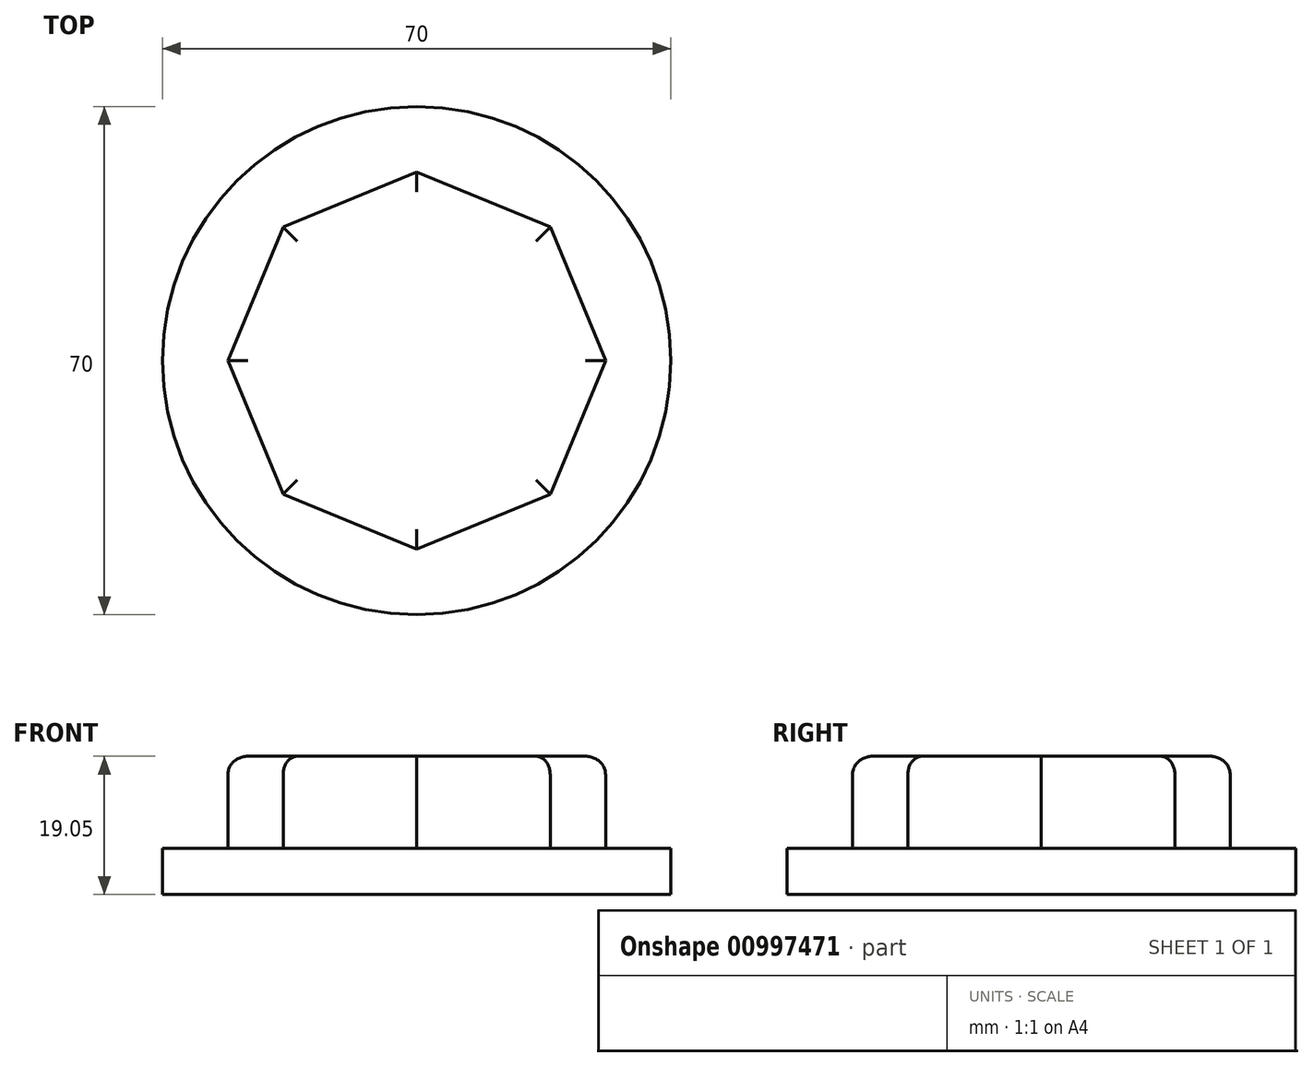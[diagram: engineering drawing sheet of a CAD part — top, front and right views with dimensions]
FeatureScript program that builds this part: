
annotation { "Feature Type Name" : "Feature", "Feature Type Description" : "" }
export const myFeature = defineFeature(function(context is Context, id is Id, definition is map)
    precondition{}
    {
        {
            var Q0;
            Q0=qCreatedBy(makeId("Top.planeOp"),FACE);
            var sketch = newSketch(context, id + "F0", { "sketchPlane" : qUnion([Q0])});
            skCircle(sketch, "E0", {"center": v(0, 0) * mm, "radius": 35 * mm});
            skSolve(sketch);
        }
        {
            var Q0;
            Q0 = qSketchRegion(id + "F0", true);
            extrude(context, id + "F1", {"entities" : qUnion([Q0]), "depth" : 6.35 * mm, "offsetDistance" : 25.4 * mm});
        }
        {
            var Q0;
            Q0=makeQuery(id+"F1.opExtrude","CAP_FACE",FACE,{"disambiguationData":[OSD([sQuery(id+"F0.wireOp",EDGE,"E0")])],"isStart":false});
            var sketch = newSketch(context, id + "F2", { "sketchPlane" : qUnion([Q0])});
            skCircle(sketch, "E1.cCircle", {"center": v(0, 0) * mm, "radius": 26 * mm, "construction": true});
            skLineSegment(sketch, "E1.0", {"start": v(26, 0) * mm, "end": v(18.38, -18.38) * mm});
            skLineSegment(sketch, "E1.1", {"start": v(18.38, -18.38) * mm, "end": v(0, -26) * mm});
            skLineSegment(sketch, "E1.2", {"start": v(0, -26) * mm, "end": v(-18.38, -18.38) * mm});
            skLineSegment(sketch, "E1.3", {"start": v(-18.38, -18.38) * mm, "end": v(-26, 0) * mm});
            skLineSegment(sketch, "E1.4", {"start": v(-26, 0) * mm, "end": v(-18.38, 18.38) * mm});
            skLineSegment(sketch, "E1.5", {"start": v(-18.38, 18.38) * mm, "end": v(0, 26) * mm});
            skLineSegment(sketch, "E1.6", {"start": v(0, 26) * mm, "end": v(18.38, 18.38) * mm});
            skLineSegment(sketch, "E1.7", {"start": v(18.38, 18.38) * mm, "end": v(26, 0) * mm});
            skSolve(sketch);
        }
        {
            var Q0;
            Q0 = qSketchRegion(id + "F2", true);
            extrude(context, id + "F3", {"entities" : qUnion([Q0]), "operationType" : NewBodyOperationType.ADD, "depth" : 12.7 * mm, "offsetDistance" : 25.4 * mm});
        }
        {
            var Q0;
            Q0=makeQuery(id+"F3.opExtrude","CAP_EDGE",EDGE,{"disambiguationData":[OSD([sQuery(id+"F2.wireOp",EDGE,"E1.0")])],"isStart":false});
            var Q1;
            Q1=makeQuery(id+"F3.opExtrude","CAP_EDGE",EDGE,{"disambiguationData":[OSD([sQuery(id+"F2.wireOp",EDGE,"E1.7")])],"isStart":false});
            var Q2;
            Q2=makeQuery(id+"F3.opExtrude","CAP_EDGE",EDGE,{"disambiguationData":[OSD([sQuery(id+"F2.wireOp",EDGE,"E1.6")])],"isStart":false});
            var Q3;
            Q3=makeQuery(id+"F3.opExtrude","CAP_EDGE",EDGE,{"disambiguationData":[OSD([sQuery(id+"F2.wireOp",EDGE,"E1.5")])],"isStart":false});
            var Q4;
            Q4=makeQuery(id+"F3.opExtrude","CAP_EDGE",EDGE,{"disambiguationData":[OSD([sQuery(id+"F2.wireOp",EDGE,"E1.1")])],"isStart":false});
            var Q5;
            Q5=makeQuery(id+"F3.opExtrude","CAP_EDGE",EDGE,{"disambiguationData":[OSD([sQuery(id+"F2.wireOp",EDGE,"E1.2")])],"isStart":false});
            var Q6;
            Q6=makeQuery(id+"F3.opExtrude","CAP_EDGE",EDGE,{"disambiguationData":[OSD([sQuery(id+"F2.wireOp",EDGE,"E1.3")])],"isStart":false});
            var Q7;
            Q7=makeQuery(id+"F3.opExtrude","CAP_EDGE",EDGE,{"disambiguationData":[OSD([sQuery(id+"F2.wireOp",EDGE,"E1.4")])],"isStart":false});
            fillet(context, id + "F4", {"entities" : qUnion([Q0, Q1, Q2, Q3, Q4, Q5, Q6, Q7]), "radius" : 2.54 * mm, "tangentPropagation" : true, "allowEdgeOverflow" : false});
        }
    });
